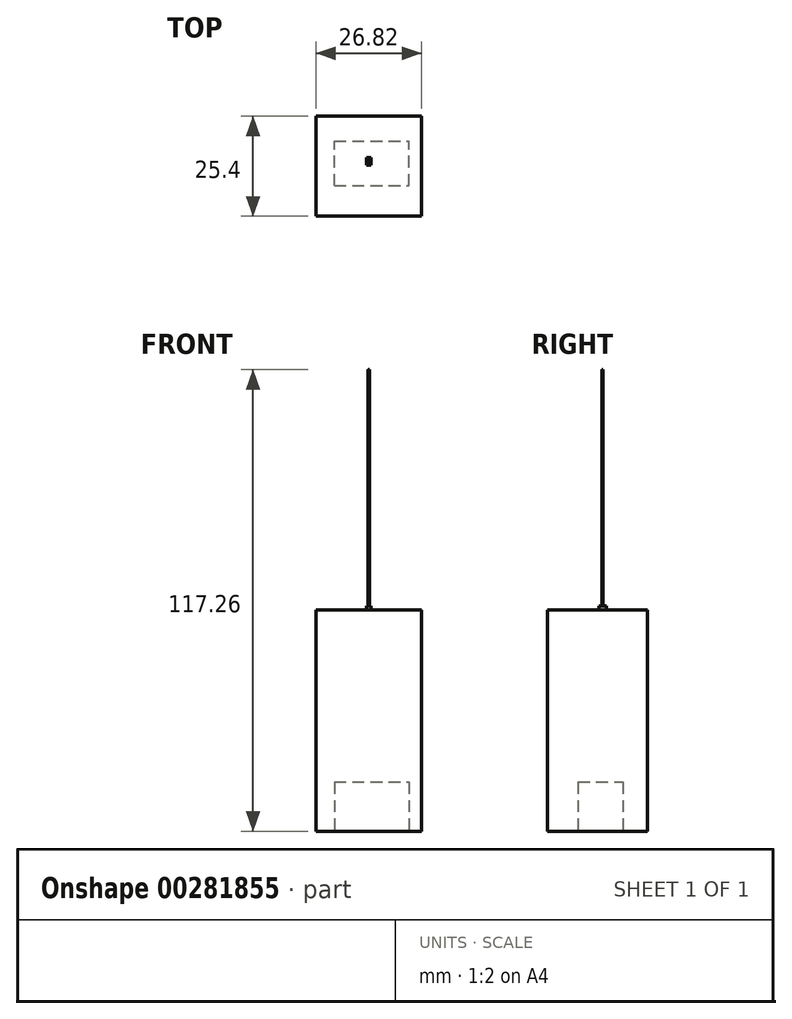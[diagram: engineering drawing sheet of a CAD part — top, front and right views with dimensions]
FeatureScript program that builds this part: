
annotation { "Feature Type Name" : "Feature", "Feature Type Description" : "" }
export const myFeature = defineFeature(function(context is Context, id is Id, definition is map)
    precondition{}
    {
        {
            var Q0;
            Q0=qCreatedBy(makeId("Front.planeOp"),FACE);
            var sketch = newSketch(context, id + "F0", { "sketchPlane" : qUnion([Q0])});
            skPoint(sketch, "E0.middle", {"position": v(0, 0) * mm});
            skLineSegment(sketch, "E1.bottom", {"start": v(13.4, -28.13) * mm, "end": v(-13.4, -28.13) * mm});
            skLineSegment(sketch, "E1.top", {"start": v(13.4, 28.13) * mm, "end": v(-13.4, 28.13) * mm});
            skLineSegment(sketch, "E1.left", {"start": v(13.4, -28.13) * mm, "end": v(13.4, 28.13) * mm});
            skLineSegment(sketch, "E1.right", {"start": v(-13.4, -28.13) * mm, "end": v(-13.4, 28.13) * mm});
            skSolve(sketch);
        }
        {
            var Q0;
            Q0=makeQuery(id+"F0.imprint","IMPRINT",FACE,{"disambiguationData":[TD([[makeQuery(id+"F0.imprint","IMPRINT",EDGE,{"derivedFrom":sQuery(id+"F0.wireOp",EDGE,"E0.bottom")}),-1.0]])]});
            var Q1;
            Q1=makeQuery(id+"F0.imprint","IMPRINT",FACE,{"disambiguationData":[TD([[makeQuery(id+"F0.imprint","IMPRINT",EDGE,{"derivedFrom":sQuery(id+"F0.wireOp",EDGE,"6NmR01IR-eKCg-eYz6-2mmr-LBdU0naWhIec.bottom")}),-1.0]])]});
            var Q2;
            Q2=makeQuery(id+"F0.imprint","IMPRINT",FACE,{"disambiguationData":[TD([[makeQuery(id+"F0.imprint","IMPRINT",EDGE,{"derivedFrom":sQuery(id+"F0.wireOp",EDGE,"E1.bottom")}),-1.0]])]});
            extrude(context, id + "F1", {"entities" : qUnion([Q0, Q1, Q2]), "depth" : 25.4 * mm});
        }
        {
            var Q0;
            Q0=makeQuery(id+"F1.opExtrude","SWEPT_FACE",FACE,{"disambiguationData":[OSD([sQuery(id+"F0.wireOp",EDGE,"E1.bottom")])]});
            var sketch = newSketch(context, id + "F2", { "sketchPlane" : qUnion([Q0])});
            skLineSegment(sketch, "E2.bottom", {"start": v(-8.74, 17.63) * mm, "end": v(10.2, 17.63) * mm});
            skLineSegment(sketch, "E2.top", {"start": v(-8.74, 6.27) * mm, "end": v(10.2, 6.27) * mm});
            skLineSegment(sketch, "E2.left", {"start": v(-8.74, 17.63) * mm, "end": v(-8.74, 6.27) * mm});
            skLineSegment(sketch, "E2.right", {"start": v(10.2, 17.63) * mm, "end": v(10.2, 6.27) * mm});
            skSolve(sketch);
        }
        {
            var Q0;
            Q0=makeQuery(id+"F2.imprint","IMPRINT",FACE,{"disambiguationData":[TD([[makeQuery(id+"F2.imprint","IMPRINT",EDGE,{"derivedFrom":sQuery(id+"F2.wireOp",EDGE,"E2.bottom")}),-1.0]])]});
            extrude(context, id + "F3", {"entities" : qUnion([Q0]), "operationType" : NewBodyOperationType.REMOVE, "endBound" : BoundingType.SYMMETRIC, "oppositeDirection" : true, "depth" : 25 * mm});
        }
        {
            var Q0;
            Q0=makeQuery(id+"F1.opExtrude","SWEPT_FACE",FACE,{"disambiguationData":[OSD([sQuery(id+"F0.wireOp",EDGE,"E1.top")])]});
            var sketch = newSketch(context, id + "F4", { "sketchPlane" : qUnion([Q0])});
            skLineSegment(sketch, "E3.bottom", {"start": v(-0.62, -12.39) * mm, "end": v(0.62, -12.39) * mm});
            skLineSegment(sketch, "E3.top", {"start": v(-0.62, -10.46) * mm, "end": v(0.62, -10.46) * mm});
            skLineSegment(sketch, "E3.left", {"start": v(-0.62, -12.39) * mm, "end": v(-0.62, -10.46) * mm});
            skLineSegment(sketch, "E3.right", {"start": v(0.62, -12.39) * mm, "end": v(0.62, -10.46) * mm});
            skPoint(sketch, "E3.middle", {"position": v(0, -11.43) * mm});
            skSolve(sketch);
        }
        {
            var Q0;
            Q0=makeQuery(id+"F4.imprint","IMPRINT",FACE,{"disambiguationData":[TD([[makeQuery(id+"F4.imprint","IMPRINT",EDGE,{"derivedFrom":sQuery(id+"F4.wireOp",EDGE,"E3.bottom")}),1.0]])]});
            extrude(context, id + "F5", {"entities" : qUnion([Q0]), "operationType" : NewBodyOperationType.ADD, "depth" : 1 * mm});
        }
        {
            var Q0;
            Q0=makeQuery(id+"F5.opExtrude","CAP_FACE",FACE,{"disambiguationData":[OSD([sQuery(id+"F4.wireOp",EDGE,"E3.bottom"),sQuery(id+"F4.wireOp",EDGE,"E3.top"),sQuery(id+"F4.wireOp",EDGE,"E3.left"),sQuery(id+"F4.wireOp",EDGE,"E3.right")])],"isStart":false});
            var sketch = newSketch(context, id + "F6", { "sketchPlane" : qUnion([Q0])});
            skCircle(sketch, "E4", {"center": v(0, -11.41) * mm, "radius": 0.14 * mm});
            skSolve(sketch);
        }
        {
            var Q0;
            Q0=makeQuery(id+"F6.imprint","IMPRINT",FACE,{"disambiguationData":[TD([[makeQuery(id+"F6.imprint","IMPRINT",EDGE,{"derivedFrom":sQuery(id+"F6.wireOp",EDGE,"E4")}),1.0]])]});
            var Q1;
            Q1=sQuery(id+"F6.wireOp",EDGE,"E4");
            extrude(context, id + "F7", {"entities" : qUnion([Q0]), "operationType" : NewBodyOperationType.ADD, "surfaceEntities" : qUnion([Q1]), "depth" : 60 * mm});
        }
    });
